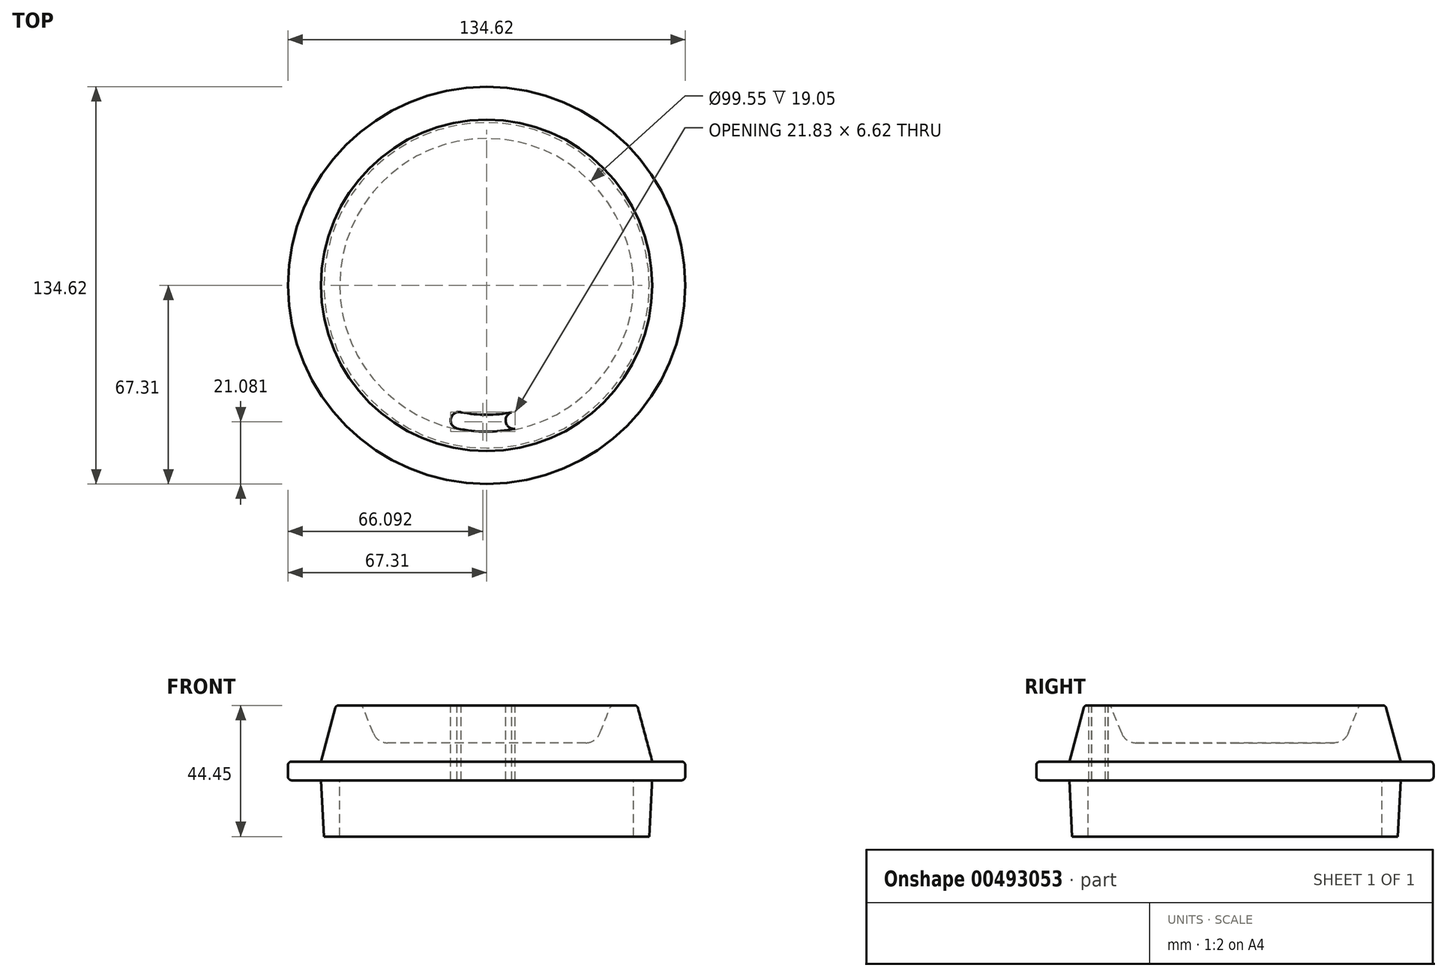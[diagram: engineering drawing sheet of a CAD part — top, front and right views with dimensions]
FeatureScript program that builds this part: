
annotation { "Feature Type Name" : "Feature", "Feature Type Description" : "" }
export const myFeature = defineFeature(function(context is Context, id is Id, definition is map)
    precondition{}
    {
        {
            var Q0;
            Q0=qCreatedBy(makeId("Top.planeOp"),FACE);
            var sketch = newSketch(context, id + "F0", { "sketchPlane" : qUnion([Q0])});
            skCircle(sketch, "E0", {"center": v(0, 0) * mm, "radius": 67.31 * mm});
            skCircle(sketch, "E1", {"center": v(0, 0) * mm, "radius": 56.12 * mm});
            skCircle(sketch, "E2", {"center": v(0, 0) * mm, "radius": 49.77 * mm});
            skCircle(sketch, "E3", {"center": v(0, 0) * mm, "radius": 37.07 * mm});
            skCircle(sketch, "E4", {"center": v(0, 0) * mm, "radius": 43.42 * mm});
            skSolve(sketch);
        }
        {
            var Q0;
            Q0=makeQuery(id+"F0.imprint","IMPRINT",FACE,{"disambiguationData":[TD([[makeQuery(id+"F0.imprint","IMPRINT",EDGE,{"derivedFrom":sQuery(id+"F0.wireOp",EDGE,"E0")}),1.0]])]});
            extrude(context, id + "F1", {"entities" : qUnion([Q0]), "depth" : 6.35 * mm});
        }
        {
            var Q0;
            Q0=makeQuery(id+"F0.imprint","IMPRINT",FACE,{"disambiguationData":[TD([[makeQuery(id+"F0.imprint","IMPRINT",EDGE,{"derivedFrom":sQuery(id+"F0.wireOp",EDGE,"E1")}),1.0]])]});
            extrude(context, id + "F2", {"entities" : qUnion([Q0]), "oppositeDirection" : true, "depth" : 19.05 * mm});
        }
        {
            var Q0;
            Q0=makeQuery(id+"F0.imprint","IMPRINT",FACE,{"disambiguationData":[TD([[makeQuery(id+"F0.imprint","IMPRINT",EDGE,{"derivedFrom":sQuery(id+"F0.wireOp",EDGE,"E2")}),1.0]])]});
            var Q1;
            Q1=makeQuery(id+"F0.imprint","IMPRINT",FACE,{"disambiguationData":[TD([[makeQuery(id+"F0.imprint","IMPRINT",EDGE,{"derivedFrom":sQuery(id+"F0.wireOp",EDGE,"E1")}),1.0]])]});
            var Q2;
            Q2=makeQuery(id+"F0.imprint","IMPRINT",FACE,{"disambiguationData":[TD([[makeQuery(id+"F0.imprint","IMPRINT",EDGE,{"derivedFrom":sQuery(id+"F0.wireOp",EDGE,"E3")}),-1.0]])]});
            extrude(context, id + "F3", {"entities" : qUnion([Q0, Q1, Q2]), "operationType" : NewBodyOperationType.ADD, "depth" : 25.4 * mm});
        }
        {
            var Q0;
            Q0=makeQuery(id+"F2.opExtrude","CAP_EDGE",EDGE,{"disambiguationData":[OSD([sQuery(id+"F0.wireOp",EDGE,"E1")])],"isStart":false});
            chamfer(context, id + "F4", {"entities" : qUnion([Q0]), "chamferType" : ChamferType.OFFSET_ANGLE, "width" : 19.05 * mm, "oppositeDirection" : false, "angle" : 3 * degree, "tangentPropagation" : true});
        }
        {
            var Q0;
            Q0=makeQuery(id+"F3.opExtrude","CAP_EDGE",EDGE,{"disambiguationData":[OSD([sQuery(id+"F0.wireOp",EDGE,"E1")])],"isStart":false});
            chamfer(context, id + "F5", {"entities" : qUnion([Q0]), "chamferType" : ChamferType.TWO_OFFSETS, "width1" : 5.08 * mm, "oppositeDirection" : false, "width2" : 19.05 * mm, "tangentPropagation" : true});
        }
        {
            var Q0;
            Q0=makeQuery(id+"F3.opExtrude","CAP_EDGE",EDGE,{"disambiguationData":[OSD([sQuery(id+"F0.wireOp",EDGE,"E3")])],"isStart":false});
            chamfer(context, id + "F6", {"entities" : qUnion([Q0]), "chamferType" : ChamferType.TWO_OFFSETS, "width1" : 5.08 * mm, "oppositeDirection" : true, "width2" : 12.7 * mm, "tangentPropagation" : true});
        }
        {
            var Q0;
            Q0=makeQuery(id+"F0.imprint","IMPRINT",FACE,{"disambiguationData":[TD([[makeQuery(id+"F0.imprint","IMPRINT",EDGE,{"derivedFrom":sQuery(id+"F0.wireOp",EDGE,"E3")}),1.0]])]});
            extrude(context, id + "F7", {"entities" : qUnion([Q0]), "operationType" : NewBodyOperationType.ADD, "depth" : 12.7 * mm});
        }
        {
            var Q0;
            Q0=makeQuery(id+"F3.opExtrude","CAP_FACE",FACE,{"disambiguationData":[OSD([sQuery(id+"F0.wireOp",EDGE,"E1"),sQuery(id+"F0.wireOp",EDGE,"E3")])],"isStart":false});
            var sketch = newSketch(context, id + "F8", { "sketchPlane" : qUnion([Q0])});
            skLineSegment(sketch, "E5", {"start": v(-10.91, -40.72) * mm, "end": v(-13.21, -49.3) * mm});
            skLineSegment(sketch, "E6", {"start": v(-21.96, -46.96) * mm, "end": v(-4.46, -51.65) * mm});
            skLineSegment(sketch, "E7", {"start": v(-11.32, -42.25) * mm, "end": v(-5.8, -43.73) * mm});
            skLineSegment(sketch, "E8", {"start": v(-5.8, -43.73) * mm, "end": v(-7.28, -49.25) * mm});
            skLineSegment(sketch, "E9", {"start": v(-7.28, -49.25) * mm, "end": v(-12.8, -47.77) * mm});
            skCircle(sketch, "E10", {"center": v(-9.3, -45.75) * mm, "radius": 2.86 * mm});
            skPoint(sketch, "E10.centerSnap0", {"position": v(-12.06, -45.01) * mm});
            skLineSegment(sketch, "E11", {"start": v(-6.54, -46.5) * mm, "end": v(-9.3, -45.75) * mm});
            skLineSegment(sketch, "E12", {"start": v(-9.3, -45.75) * mm, "end": v(-12.06, -45.01) * mm});
            skCircle(sketch, "E13.MirrorC", {"center": v(9.3, -45.75) * mm, "radius": 2.86 * mm});
            skArc(sketch, "E14", {"start": v(-8.56, -43) * mm, "mid": v(0, -43.84) * mm, "end": v(8.56, -43) * mm});
            skPoint(sketch, "E14.endSnap0", {"position": v(-8.56, -43) * mm});
            skArc(sketch, "E15", {"start": v(-10.04, -48.51) * mm, "mid": v(0, -49.54) * mm, "end": v(10.04, -48.51) * mm});
            skPoint(sketch, "E15.endSnap0", {"position": v(-10.04, -48.51) * mm});
            skSolve(sketch);
        }
        {
            var Q0;
            {var subQ3=sQuery(id+"F8.wireOp",EDGE,"E11");Q0=makeQuery(id+"F8.imprint","IMPRINT",FACE,{"disambiguationData":[TD([[makeQuery(id+"F8.imprint","IMPRINT",EDGE,{"derivedFrom":subQ3}),-1.0]])]});}
            var Q1;
            {var subQ7=sQuery(id+"F8.wireOp",EDGE,"E14");Q1=makeQuery(id+"F8.imprint","IMPRINT",FACE,{"disambiguationData":[TD([[makeQuery(id+"F8.imprint","IMPRINT",EDGE,{"derivedFrom":subQ7}),-1.0]])]});}
            var Q2;
            {var subQ0=sQuery(id+"F8.wireOp",EDGE,"E11");Q2=makeQuery(id+"F8.imprint","IMPRINT",FACE,{"disambiguationData":[TD([[makeQuery(id+"F8.imprint","IMPRINT",EDGE,{"derivedFrom":subQ0}),1.0]])]});}
            var Q3;
            {var subQ0=sQuery(id+"F8.wireOp",EDGE,"E8");var subQ1=sQuery(id+"F8.wireOp",EDGE,"E7");var subQ2=makeQuery(id+"F8.imprint","INTERSECT",VERTEX,{"derivedFrom":[subQ1,subQ0]});Q3=makeQuery(id+"F8.imprint","IMPRINT",FACE,{"disambiguationData":[TD([[makeQuery(id+"F8.imprint","IMPRINT",EDGE,{"disambiguationData":[TD([[subQ2,1.0]])],"derivedFrom":subQ1}),-1.0]])]});}
            var Q4;
            {var subQ1=sQuery(id+"F8.wireOp",EDGE,"E8");var subQ3=sQuery(id+"F8.wireOp",EDGE,"E15");var subQ4=makeQuery(id+"F8.imprint","INTERSECT",VERTEX,{"derivedFrom":[subQ1,subQ3]});Q4=makeQuery(id+"F8.imprint","IMPRINT",FACE,{"disambiguationData":[TD([[makeQuery(id+"F8.imprint","IMPRINT",EDGE,{"disambiguationData":[TD([[subQ4,1.0]])],"derivedFrom":subQ3}),1.0]])]});}
            var Q5;
            {var subQ0=sQuery(id+"F8.wireOp",EDGE,"E13.MirrorC");var subQ1=makeQuery(id+"F8.imprint","INTERSECT",VERTEX,{"derivedFrom":[subQ0,sQuery(id+"F8.wireOp",EDGE,"E14")]});Q5=makeQuery(id+"F8.imprint","IMPRINT",FACE,{"disambiguationData":[TD([[makeQuery(id+"F8.imprint","IMPRINT",EDGE,{"disambiguationData":[TD([[subQ1,-1.0]])],"derivedFrom":subQ0}),-1.0]])]});}
            extrude(context, id + "F9", {"entities" : qUnion([Q0, Q1, Q2, Q3, Q4, Q5]), "operationType" : NewBodyOperationType.REMOVE, "oppositeDirection" : true, "depth" : 127 * mm});
        }
        {
            var Q0;
            Q0=makeQuery(id+"F1.opExtrude","CAP_EDGE",EDGE,{"disambiguationData":[OSD([sQuery(id+"F0.wireOp",EDGE,"E0")])],"isStart":false});
            var Q1;
            {var subQ0=sQuery(id+"F0.wireOp",EDGE,"E1");Q1=makeQuery(id+"F5.opChamfer","BLEND_EDGE",EDGE,{"blendedFrom":[makeQuery(id+"F3.opExtrude","CAP_EDGE",EDGE,{"disambiguationData":[OSD([subQ0])],"isStart":false}),makeQuery(id+"F3.opExtrude","CAP_FACE",FACE,{"disambiguationData":[OSD([subQ0,sQuery(id+"F0.wireOp",EDGE,"E3")])],"isStart":false})],"blendedInto":[makeQuery(id+"F3.opExtrude","CAP_FACE",FACE,{"disambiguationData":[OSD([subQ0,sQuery(id+"F0.wireOp",EDGE,"E3")])],"isStart":false})]});}
            var Q2;
            Q2=makeQuery(id+"F1.opExtrude","CAP_EDGE",EDGE,{"disambiguationData":[OSD([sQuery(id+"F0.wireOp",EDGE,"E0")])],"isStart":true});
            var Q3;
            {var subQ0=sQuery(id+"F0.wireOp",EDGE,"E3");Q3=makeQuery(id+"F6.opChamfer","BLEND_EDGE",EDGE,{"blendedFrom":[makeQuery(id+"F3.opExtrude","CAP_EDGE",EDGE,{"disambiguationData":[OSD([subQ0])],"isStart":false}),makeQuery(id+"F3.opExtrude","CAP_FACE",FACE,{"disambiguationData":[OSD([sQuery(id+"F0.wireOp",EDGE,"E1"),subQ0])],"isStart":false})],"blendedInto":[makeQuery(id+"F3.opExtrude","CAP_FACE",FACE,{"disambiguationData":[OSD([sQuery(id+"F0.wireOp",EDGE,"E1"),subQ0])],"isStart":false})]});}
            fillet(context, id + "F10", {"entities" : qUnion([Q0, Q1, Q2, Q3]), "radius" : 1.27 * mm, "tangentPropagation" : true, "allowEdgeOverflow" : false});
        }
        {
            var Q0;
            {var subQ0=sQuery(id+"F0.wireOp",EDGE,"E3");Q0=makeQuery(id+"F7.boolean.opBoolean","MERGE",EDGE,{"derivedFrom":[makeQuery(id+"F6.opChamfer","BLEND_EDGE",EDGE,{"blendedFrom":[makeQuery(id+"F3.opExtrude","CAP_EDGE",EDGE,{"disambiguationData":[OSD([subQ0])],"isStart":false}),makeQuery(id+"F3.opExtrude","SWEPT_FACE",FACE,{"disambiguationData":[OSD([subQ0])]})],"blendedInto":[makeQuery(id+"F3.opExtrude","SWEPT_FACE",FACE,{"disambiguationData":[OSD([subQ0])]})]}),makeQuery(id+"F7.opExtrude","CAP_EDGE",EDGE,{"disambiguationData":[OSD([subQ0])],"isStart":false})]});}
            fillet(context, id + "F11", {"entities" : qUnion([Q0]), "radius" : 5.08 * mm, "tangentPropagation" : true, "allowEdgeOverflow" : false});
        }
    });
